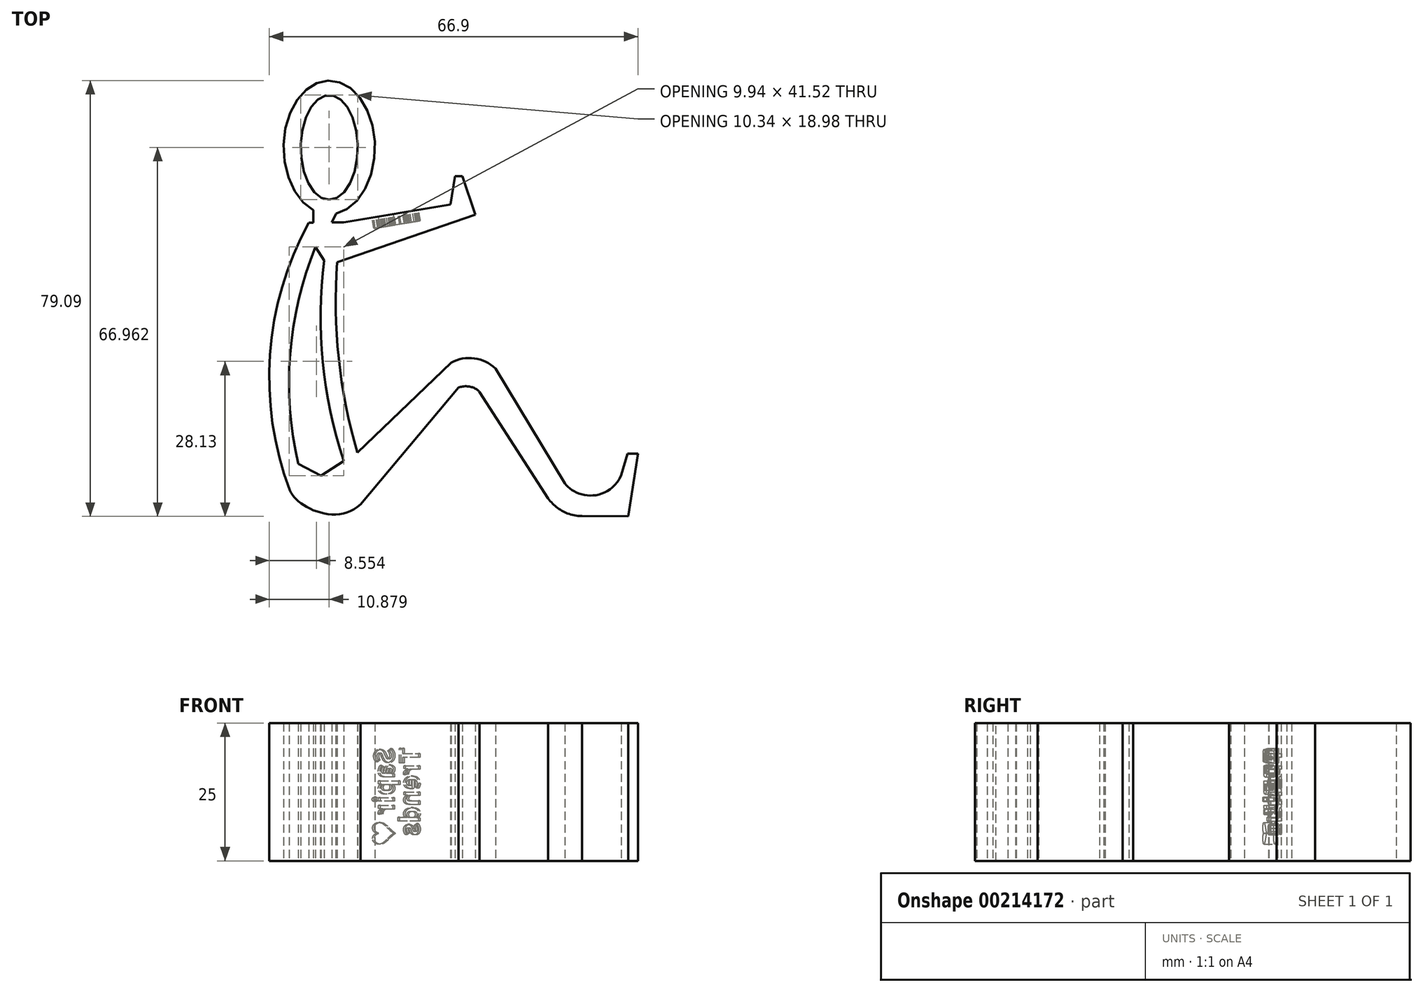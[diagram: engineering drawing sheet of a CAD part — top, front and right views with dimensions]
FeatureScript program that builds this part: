
annotation { "Feature Type Name" : "Feature", "Feature Type Description" : "" }
export const myFeature = defineFeature(function(context is Context, id is Id, definition is map)
    precondition{}
    {
        {
            var Q0;
            Q0=qCreatedBy(makeId("Top.planeOp"),FACE);
            var sketch = newSketch(context, id + "F0", { "sketchPlane" : qUnion([Q0])});
            skEllipse(sketch, "E0", {"center": v(-1.45, 30.92) * mm, "majorRadius": 9.49 * mm, "minorRadius": 5.17 * mm, "majorAxis": v(0, -1)});
            skEllipse(sketch, "E1", {"center": v(-1.45, 30.92) * mm, "majorRadius": 12.13 * mm, "minorRadius": 8.3 * mm, "majorAxis": v(0, -1)});
            skArc(sketch, "E2", {"start": v(-5.18, 17.23) * mm, "mid": v(-12.19, -6.66) * mm, "end": v(-8.6, -31.3) * mm});
            skArc(sketch, "E3", {"start": v(-3.97, 12.85) * mm, "mid": v(-8.55, -6.58) * mm, "end": v(-7.05, -26.48) * mm});
            skArc(sketch, "E4", {"start": v(-2.38, 10.39) * mm, "mid": v(-2.65, -8) * mm, "end": v(1.2, -25.98) * mm});
            skArc(sketch, "E5", {"start": v(0, 10.07) * mm, "mid": v(0.28, -7.36) * mm, "end": v(3.68, -24.45) * mm});
            skArc(sketch, "E6", {"start": v(28.72, -9.21) * mm, "mid": v(24.88, -7.36) * mm, "end": v(20.68, -8.12) * mm});
            skFitSpline(sketch, "E7", {"points": [v(22.03, -12.68) * mm, v(25.82, -13.45) * mm], "startDerivative": vector(4.24, 1.93) * mm, "endDerivative": vector(1.54, -2.31) * mm});
            skFitSpline(sketch, "E8", {"points": [v(38.26, -32.78) * mm, v(44.43, -35.98) * mm], "startDerivative": vector(4.8, -5.79) * mm, "endDerivative": vector(8.76, -0.33) * mm});
            skFitSpline(sketch, "E9", {"points": [v(41.34, -30.03) * mm, v(51.54, -28.55) * mm], "startDerivative": vector(5.12, -7.77) * mm, "endDerivative": vector(7.44, 15.87) * mm});
            skLineSegment(sketch, "E10", {"start": v(28.72, -9.21) * mm, "end": v(41.34, -30.03) * mm});
            skLineSegment(sketch, "E11", {"start": v(52.7, -24.63) * mm, "end": v(54.57, -24.63) * mm});
            skLineSegment(sketch, "E12", {"start": v(54.57, -24.63) * mm, "end": v(52.8, -36.04) * mm});
            skLineSegment(sketch, "E13", {"start": v(52.8, -36.04) * mm, "end": v(44.43, -35.98) * mm});
            skLineSegment(sketch, "E14", {"start": v(51.54, -28.55) * mm, "end": v(52.7, -24.63) * mm});
            skLineSegment(sketch, "E15", {"start": v(38.26, -32.78) * mm, "end": v(25.82, -13.45) * mm});
            skLineSegment(sketch, "E16", {"start": v(22.03, -12.68) * mm, "end": v(4.2, -33.83) * mm});
            skLineSegment(sketch, "E17", {"start": v(20.68, -8.12) * mm, "end": v(3.68, -24.45) * mm});
            skLineSegment(sketch, "E18", {"start": v(1.2, -25.98) * mm, "end": v(-2.94, -28.67) * mm});
            skLineSegment(sketch, "E19", {"start": v(-2.94, -28.67) * mm, "end": v(-7.05, -26.48) * mm});
            skLineSegment(sketch, "E20", {"start": v(-3.97, 12.85) * mm, "end": v(-2.38, 10.39) * mm});
            skLineSegment(sketch, "E21", {"start": v(0, 10.07) * mm, "end": v(25.04, 18.72) * mm});
            skLineSegment(sketch, "E22", {"start": v(25.04, 18.72) * mm, "end": v(22.7, 25.72) * mm});
            skLineSegment(sketch, "E23", {"start": v(22.7, 25.72) * mm, "end": v(21.38, 25.72) * mm});
            skLineSegment(sketch, "E24", {"start": v(21.38, 25.72) * mm, "end": v(20.55, 20.58) * mm});
            skLineSegment(sketch, "E25", {"start": v(20.55, 20.58) * mm, "end": v(1.2, 17.33) * mm});
            skLineSegment(sketch, "E26", {"start": v(1.2, 17.33) * mm, "end": v(-0.97, 17.33) * mm});
            skLineSegment(sketch, "E27", {"start": v(-0.97, 17.33) * mm, "end": v(-0.22, 18.92) * mm});
            skLineSegment(sketch, "E28", {"start": v(-5.18, 17.23) * mm, "end": v(-4.33, 17.23) * mm});
            skLineSegment(sketch, "E29", {"start": v(-4.33, 17.23) * mm, "end": v(-4.33, 19.55) * mm});
            skLineSegment(sketch, "E30", {"start": v(22.7, 25.72) * mm, "end": v(41.34, -30.03) * mm, "construction": true});
            skLineSegment(sketch, "E31", {"start": v(52.8, -36.04) * mm, "end": v(-18.74, -35.57) * mm, "construction": true});
            skFitSpline(sketch, "E32", {"points": [v(-8.6, -31.3) * mm, v(4.2, -33.83) * mm], "startDerivative": vector(3.47, -9.13) * mm, "endDerivative": vector(12.63, 12.4) * mm});
            skSolve(sketch);
        }
        {
            var Q0;
            Q0=makeQuery(id+"F0.imprint","IMPRINT",FACE,{"disambiguationData":[TD([[makeQuery(id+"F0.imprint","IMPRINT",EDGE,{"derivedFrom":sQuery(id+"F0.wireOp",EDGE,"E2")}),1.0]])]});
            var Q1;
            Q1=makeQuery(id+"F0.imprint","IMPRINT",FACE,{"disambiguationData":[TD([[makeQuery(id+"F0.imprint","IMPRINT",EDGE,{"derivedFrom":sQuery(id+"F0.wireOp",EDGE,"E0")}),-1.0]])]});
            extrude(context, id + "F1", {"entities" : qUnion([Q0, Q1]), "depth" : 25 * mm});
        }
        {
            var Q0;
            Q0=makeQuery(id+"F1.opExtrude","SWEPT_FACE",FACE,{"disambiguationData":[OSD([sQuery(id+"F0.wireOp",EDGE,"E25")])]});
            var sketch = newSketch(context, id + "F2", { "sketchPlane" : qUnion([Q0])});
            skText(sketch, "E33", { "text": "Sapir ♥\nTrends", "fontName": "NotoSansCJKsc-Bold.otf"});
            skPoint(sketch, "E34", {"position": v(-13.06, 0) * mm});
            const initialGuessF2  = {"E33": [-0.01306, 0.02057, 0, -1, 0.00337]};
            skSetInitialGuess(sketch, initialGuessF2);
            skSolve(sketch);
        }
        {
            var Q0;
            Q0 = qSketchRegion(id + "F2", true);
            extrude(context, id + "F3", {"entities" : qUnion([Q0]), "operationType" : NewBodyOperationType.REMOVE, "oppositeDirection" : true, "depth" : 2 * mm});
        }
    });
